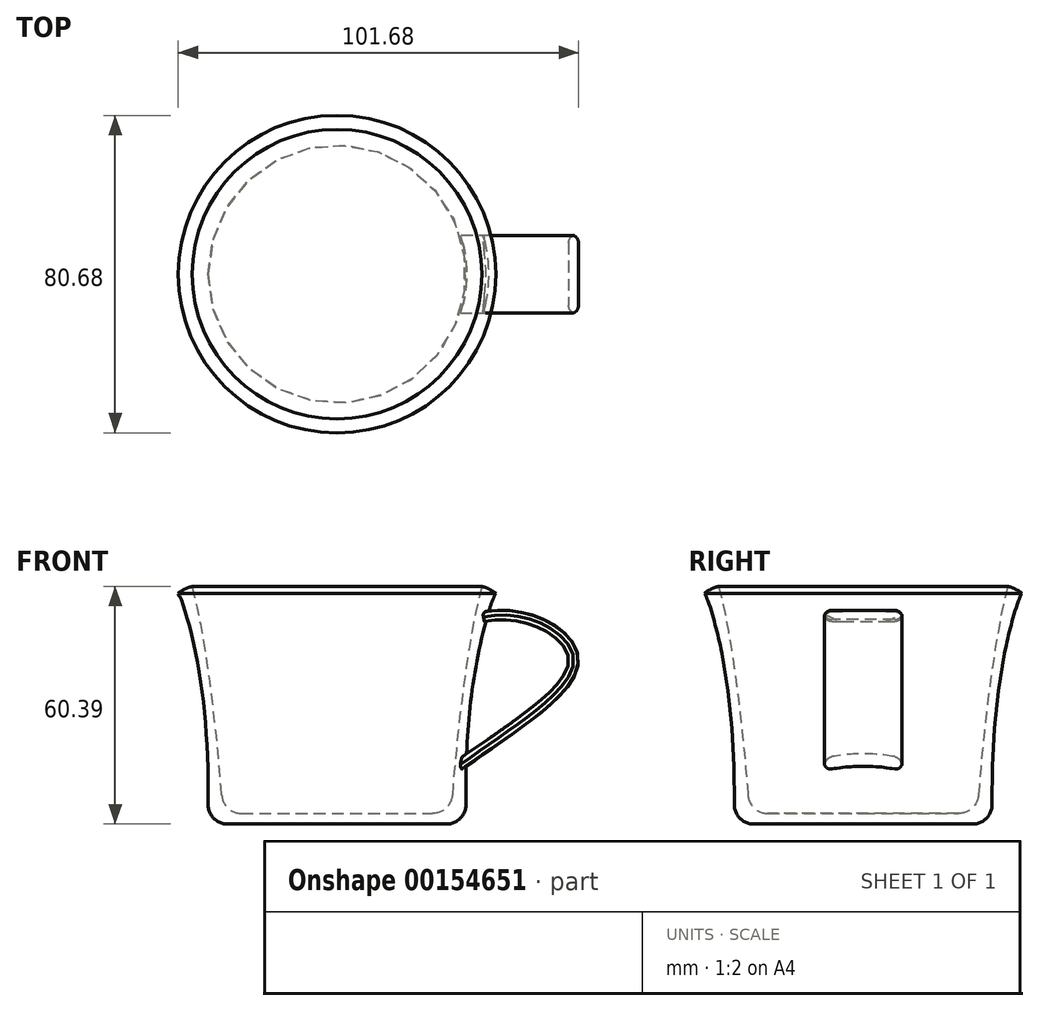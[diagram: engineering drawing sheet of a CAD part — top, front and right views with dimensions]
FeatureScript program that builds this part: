
annotation { "Feature Type Name" : "Feature", "Feature Type Description" : "" }
export const myFeature = defineFeature(function(context is Context, id is Id, definition is map)
    precondition{}
    {
        {
            var Q0;
            Q0=qCreatedBy(makeId("Front.planeOp"),FACE);
            var sketch = newSketch(context, id + "F0", { "sketchPlane" : qUnion([Q0])});
            skLineSegment(sketch, "E0", {"start": v(-27.75, 0) * mm, "end": v(0, 0) * mm});
            skLineSegment(sketch, "E1", {"start": v(0, 0) * mm, "end": v(0, 2.74) * mm});
            skLineSegment(sketch, "E2", {"start": v(0, 2.74) * mm, "end": v(-24.3, 2.74) * mm});
            skFitSpline(sketch, "E3", {"points": [v(-32.87, 0) * mm, v(-35.69, 42.26) * mm, v(-40.34, 58.61) * mm], "startDerivative": vector(2.54, 81.24) * mm, "endDerivative": vector(-8.5, 12.03) * mm});
            skFitSpline(sketch, "E4", {"points": [v(-28.97, 2.74) * mm, v(-36.79, 60.4) * mm], "startDerivative": vector(-2.5, 41.98) * mm, "endDerivative": vector(-11.76, 41.21) * mm});
            skArc(sketch, "E5", {"start": v(-36.79, 60.4) * mm, "mid": v(-38.67, 59.72) * mm, "end": v(-40.34, 58.61) * mm});
            skArc(sketch, "E6.filletArc", {"start": v(-32.75, 5.07) * mm, "mid": v(-31.31, 1.49) * mm, "end": v(-27.75, 0) * mm});
            skArc(sketch, "E7.filletArc", {"start": v(-29.28, 7.36) * mm, "mid": v(-27.7, 4.07) * mm, "end": v(-24.3, 2.74) * mm});
            skSolve(sketch);
        }
        {
            var Q0;
            Q0 = qSketchRegion(id + "F0", true);
            var Q1;
            Q1=sQuery(id+"F0.wireOp",EDGE,"E1");
            revolve(context, id + "F1", {"entities" : qUnion([Q0]), "axis" : qUnion([Q1]), "revolveType" : RevolveType.FULL});
        }
        {
            var Q0;
            Q0=qCreatedBy(makeId("Front.planeOp"),FACE);
            var sketch = newSketch(context, id + "F2", { "sketchPlane" : qUnion([Q0])});
            skFitSpline(sketch, "E8", {"points": [v(31.58, 13.83) * mm, v(61.28, 42.46) * mm, v(36.98, 53.9) * mm], "startDerivative": vector(83.87, 59.48) * mm, "endDerivative": vector(-80.38, -14.8) * mm});
            skFitSpline(sketch, "E9.0", {"points": [v(30.13, 15.87) * mm, v(33.65, 18.36) * mm, v(38.89, 21.94) * mm, v(45.22, 26.42) * mm, v(49.5, 29.64) * mm, v(53.14, 32.7) * mm, v(56.01, 35.61) * mm, v(57.62, 37.83) * mm, v(58.4, 39.43) * mm, v(58.74, 40.51) * mm, v(58.85, 41.33) * mm, v(58.83, 41.96) * mm, v(58.75, 42.58) * mm, v(58.51, 43.4) * mm, v(58, 44.45) * mm, v(57.23, 45.53) * mm, v(55.9, 46.97) * mm, v(53.66, 48.68) * mm, v(50.24, 50.36) * mm, v(46.28, 51.5) * mm, v(41.95, 51.96) * mm, v(38.94, 51.71) * mm, v(37.43, 51.44) * mm]});
            skLineSegment(sketch, "E10", {"start": v(31.58, 13.83) * mm, "end": v(30.13, 15.87) * mm});
            skLineSegment(sketch, "E11", {"start": v(37.43, 51.44) * mm, "end": v(36.98, 53.9) * mm});
            skSolve(sketch);
        }
        {
            var Q0;
            Q0 = qSketchRegion(id + "F2", true);
            extrude(context, id + "F3", {"entities" : qUnion([Q0]), "operationType" : NewBodyOperationType.ADD, "depth" : 10 * mm, "hasSecondDirection" : true, "secondDirectionOppositeDirection" : true, "secondDirectionDepth" : 10 * mm});
        }
        {
            var Q0;
            Q0=makeQuery(id+"F3.opExtrude","CAP_EDGE",EDGE,{"disambiguationData":[OSD([sQuery(id+"F2.wireOp",EDGE,"E8")])],"isStart":false});
            var Q1;
            Q1=makeQuery(id+"F3.opExtrude","CAP_EDGE",EDGE,{"disambiguationData":[OSD([sQuery(id+"F2.wireOp",EDGE,"E9.0")])],"isStart":false});
            var Q2;
            Q2=makeQuery(id+"F3.opExtrude","CAP_EDGE",EDGE,{"disambiguationData":[OSD([sQuery(id+"F2.wireOp",EDGE,"E8")])],"isStart":true});
            var Q3;
            Q3=makeQuery(id+"F3.opExtrude","CAP_EDGE",EDGE,{"disambiguationData":[OSD([sQuery(id+"F2.wireOp",EDGE,"E9.0")])],"isStart":true});
            fillet(context, id + "F4", {"entities" : qUnion([Q0, Q1, Q2, Q3]), "radius" : 2 * mm, "tangentPropagation" : true, "allowEdgeOverflow" : false});
        }
    });
